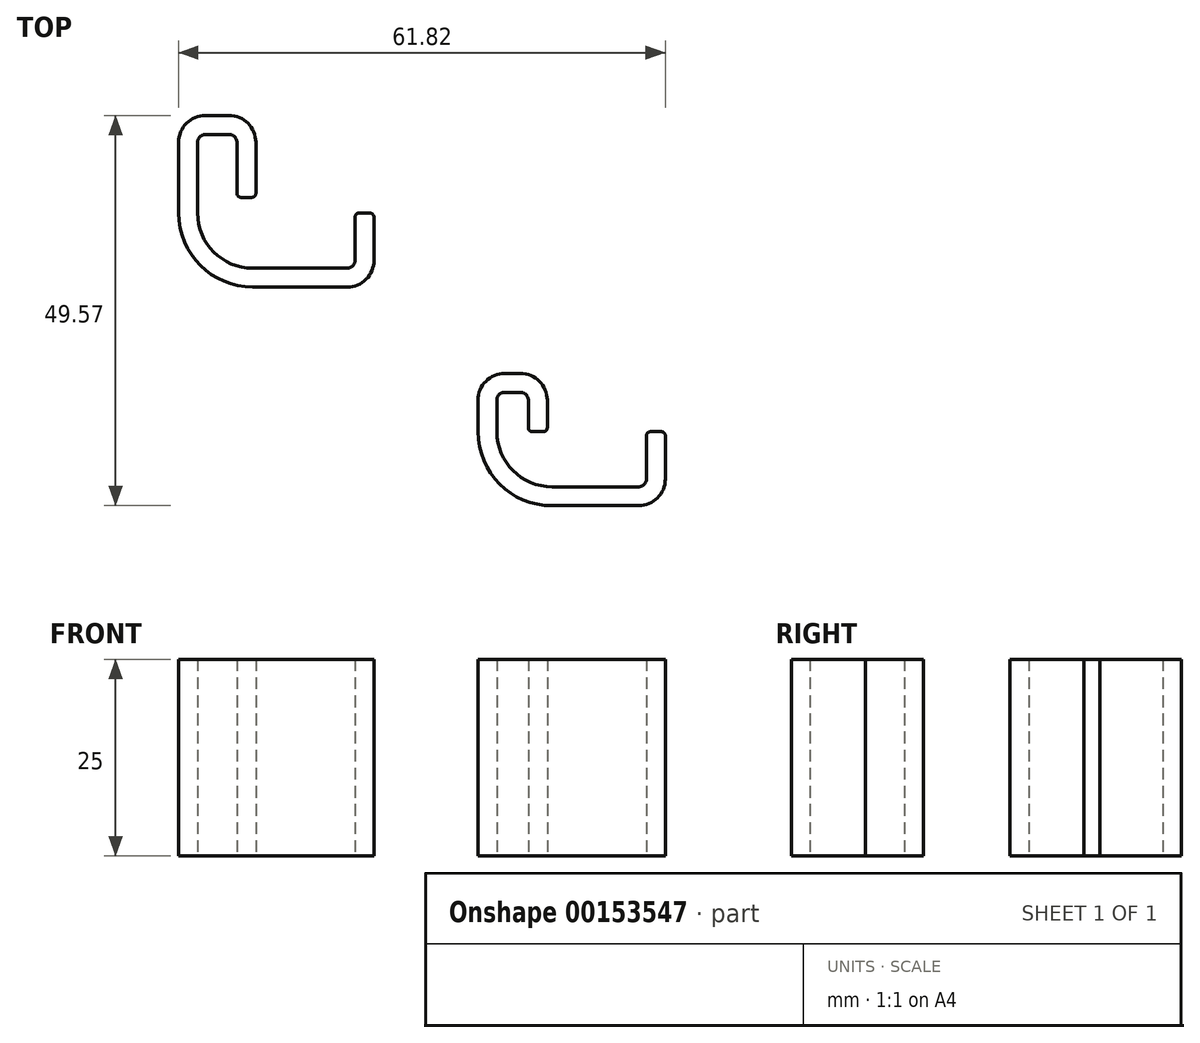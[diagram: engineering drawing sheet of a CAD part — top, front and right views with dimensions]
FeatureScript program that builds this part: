
annotation { "Feature Type Name" : "Feature", "Feature Type Description" : "" }
export const myFeature = defineFeature(function(context is Context, id is Id, definition is map)
    precondition{}
    {
        {
            var Q0;
            Q0=qCreatedBy(makeId("Top.planeOp"),FACE);
            var sketch = newSketch(context, id + "F0", { "sketchPlane" : qUnion([Q0])});
            skLineSegment(sketch, "E0", {"start": v(0, -0.5) * mm, "end": v(0, -6) * mm});
            skLineSegment(sketch, "E1", {"start": v(-1, -7) * mm, "end": v(-12, -7) * mm});
            skLineSegment(sketch, "E2", {"start": v(-15, 5) * mm, "end": v(-15, 0) * mm});
            skLineSegment(sketch, "E3", {"start": v(-15, 0.5) * mm, "end": v(-15, 4) * mm});
            skLineSegment(sketch, "E4", {"start": v(-16, 5) * mm, "end": v(-18, 5) * mm});
            skLineSegment(sketch, "E5", {"start": v(-19, 4) * mm, "end": v(-19, 0) * mm});
            skPoint(sketch, "E6.visualSharp", {"position": v(-19, -7) * mm});
            skArc(sketch, "E6.filletArc", {"start": v(-19, 0) * mm, "mid": v(-16.95, -4.95) * mm, "end": v(-12, -7) * mm});
            skPoint(sketch, "E7.visualSharp", {"position": v(-19, 5) * mm});
            skArc(sketch, "E7.filletArc", {"start": v(-18, 5) * mm, "mid": v(-18.7, 4.7) * mm, "end": v(-19, 4) * mm});
            skPoint(sketch, "E8.visualSharp", {"position": v(-15, 5) * mm});
            skArc(sketch, "E8.filletArc", {"start": v(-15, 4) * mm, "mid": v(-15.3, 4.7) * mm, "end": v(-16, 5) * mm});
            skPoint(sketch, "E9.visualSharp", {"position": v(0, -7) * mm});
            skArc(sketch, "E9.filletArc", {"start": v(-1, -7) * mm, "mid": v(-0.3, -6.7) * mm, "end": v(0, -6) * mm});
            skLineSegment(sketch, "E10.0", {"start": v(2.4, -0.5) * mm, "end": v(2.4, -6) * mm});
            skArc(sketch, "E10.1", {"start": v(-1, -9.4) * mm, "mid": v(1.4, -8.4) * mm, "end": v(2.4, -6) * mm});
            skLineSegment(sketch, "E10.2", {"start": v(-1, -9.4) * mm, "end": v(-12, -9.4) * mm});
            skArc(sketch, "E10.3", {"start": v(-21.4, 0) * mm, "mid": v(-18.65, -6.65) * mm, "end": v(-12, -9.4) * mm});
            skLineSegment(sketch, "E10.4", {"start": v(-21.4, 4) * mm, "end": v(-21.4, 0) * mm});
            skLineSegment(sketch, "E10.5", {"start": v(-12.6, 0.5) * mm, "end": v(-12.6, 4) * mm});
            skArc(sketch, "E10.6", {"start": v(-12.6, 4) * mm, "mid": v(-13.6, 6.4) * mm, "end": v(-16, 7.4) * mm});
            skLineSegment(sketch, "E10.7", {"start": v(-16, 7.4) * mm, "end": v(-18, 7.4) * mm});
            skArc(sketch, "E10.8", {"start": v(-18, 7.4) * mm, "mid": v(-20.4, 6.4) * mm, "end": v(-21.4, 4) * mm});
            skLineSegment(sketch, "E11", {"start": v(-13.1, 0) * mm, "end": v(-14.5, 0) * mm});
            skLineSegment(sketch, "E12", {"start": v(0.5, 0) * mm, "end": v(1.9, 0) * mm});
            skPoint(sketch, "E13.visualSharp", {"position": v(-15, 0) * mm});
            skArc(sketch, "E13.filletArc", {"start": v(-15, 0.5) * mm, "mid": v(-14.85, 0.15) * mm, "end": v(-14.5, 0) * mm});
            skPoint(sketch, "E14.visualSharp", {"position": v(-12.6, 0) * mm});
            skArc(sketch, "E14.filletArc", {"start": v(-13.1, 0) * mm, "mid": v(-12.75, 0.15) * mm, "end": v(-12.6, 0.5) * mm});
            skPoint(sketch, "E15.visualSharp", {"position": v(0, 0) * mm});
            skArc(sketch, "E15.filletArc", {"start": v(0.5, 0) * mm, "mid": v(0.15, -0.15) * mm, "end": v(0, -0.5) * mm});
            skPoint(sketch, "E16.visualSharp", {"position": v(2.4, 0) * mm});
            skArc(sketch, "E16.filletArc", {"start": v(2.4, -0.5) * mm, "mid": v(2.25, -0.15) * mm, "end": v(1.9, 0) * mm});
            skSolve(sketch);
        }
        {
            var Q0;
            Q0=qCreatedBy(makeId("Top.planeOp"),FACE);
            var sketch = newSketch(context, id + "F1", { "sketchPlane" : qUnion([Q0])});
            skLineSegment(sketch, "E17", {"start": v(-37.02, 27.27) * mm, "end": v(-37.02, 21.77) * mm});
            skLineSegment(sketch, "E18", {"start": v(-38.02, 20.77) * mm, "end": v(-50.02, 20.77) * mm});
            skLineSegment(sketch, "E19", {"start": v(-52.02, 37.77) * mm, "end": v(-52.02, 29.77) * mm});
            skLineSegment(sketch, "E20", {"start": v(-52.02, 30.27) * mm, "end": v(-52.02, 36.77) * mm});
            skLineSegment(sketch, "E21", {"start": v(-53.02, 37.77) * mm, "end": v(-56.02, 37.77) * mm});
            skLineSegment(sketch, "E22", {"start": v(-57.02, 36.77) * mm, "end": v(-57.02, 27.77) * mm});
            skPoint(sketch, "E23.visualSharp", {"position": v(-57.02, 20.77) * mm});
            skArc(sketch, "E23.filletArc", {"start": v(-57.02, 27.77) * mm, "mid": v(-54.97, 22.82) * mm, "end": v(-50.02, 20.77) * mm});
            skPoint(sketch, "E24.visualSharp", {"position": v(-57.02, 37.77) * mm});
            skArc(sketch, "E24.filletArc", {"start": v(-56.02, 37.77) * mm, "mid": v(-56.72, 37.48) * mm, "end": v(-57.02, 36.77) * mm});
            skPoint(sketch, "E25.visualSharp", {"position": v(-52.02, 37.77) * mm});
            skArc(sketch, "E25.filletArc", {"start": v(-52.02, 36.77) * mm, "mid": v(-52.3, 37.48) * mm, "end": v(-53.02, 37.77) * mm});
            skPoint(sketch, "E26.visualSharp", {"position": v(-37.02, 20.77) * mm});
            skArc(sketch, "E26.filletArc", {"start": v(-38.02, 20.77) * mm, "mid": v(-37.3, 21.06) * mm, "end": v(-37.02, 21.77) * mm});
            skLineSegment(sketch, "E27.0", {"start": v(-34.62, 27.27) * mm, "end": v(-34.62, 21.77) * mm});
            skArc(sketch, "E27.1", {"start": v(-38.02, 18.37) * mm, "mid": v(-35.61, 19.37) * mm, "end": v(-34.62, 21.77) * mm});
            skLineSegment(sketch, "E27.2", {"start": v(-38.02, 18.37) * mm, "end": v(-50.02, 18.37) * mm});
            skArc(sketch, "E27.3", {"start": v(-59.42, 27.77) * mm, "mid": v(-56.66, 21.12) * mm, "end": v(-50.02, 18.37) * mm});
            skLineSegment(sketch, "E27.4", {"start": v(-59.42, 36.77) * mm, "end": v(-59.42, 27.77) * mm});
            skLineSegment(sketch, "E27.5", {"start": v(-49.62, 30.27) * mm, "end": v(-49.62, 36.77) * mm});
            skArc(sketch, "E27.6", {"start": v(-49.62, 36.77) * mm, "mid": v(-50.61, 39.17) * mm, "end": v(-53.02, 40.17) * mm});
            skLineSegment(sketch, "E27.7", {"start": v(-53.02, 40.17) * mm, "end": v(-56.02, 40.17) * mm});
            skArc(sketch, "E27.8", {"start": v(-56.02, 40.17) * mm, "mid": v(-58.42, 39.17) * mm, "end": v(-59.42, 36.77) * mm});
            skLineSegment(sketch, "E28", {"start": v(-50.12, 29.77) * mm, "end": v(-51.52, 29.77) * mm});
            skLineSegment(sketch, "E29", {"start": v(-36.52, 27.77) * mm, "end": v(-35.12, 27.77) * mm});
            skPoint(sketch, "E30.visualSharp", {"position": v(-52.02, 29.77) * mm});
            skArc(sketch, "E30.filletArc", {"start": v(-52.02, 30.27) * mm, "mid": v(-51.87, 29.92) * mm, "end": v(-51.52, 29.77) * mm});
            skPoint(sketch, "E31.visualSharp", {"position": v(-49.62, 29.77) * mm});
            skArc(sketch, "E31.filletArc", {"start": v(-50.12, 29.77) * mm, "mid": v(-49.76, 29.92) * mm, "end": v(-49.62, 30.27) * mm});
            skPoint(sketch, "E32.visualSharp", {"position": v(-37.02, 27.77) * mm});
            skArc(sketch, "E32.filletArc", {"start": v(-36.52, 27.77) * mm, "mid": v(-36.87, 27.62) * mm, "end": v(-37.02, 27.27) * mm});
            skPoint(sketch, "E33.visualSharp", {"position": v(-34.62, 27.77) * mm});
            skArc(sketch, "E33.filletArc", {"start": v(-34.62, 27.27) * mm, "mid": v(-34.76, 27.62) * mm, "end": v(-35.12, 27.77) * mm});
            skSolve(sketch);
        }
        {
            var Q0;
            Q0 = qSketchRegion(id + "F0", true);
            var Q1;
            Q1 = qSketchRegion(id + "F1", true);
            extrude(context, id + "F2", {"entities" : qUnion([Q0, Q1]), "depth" : 25 * mm});
        }
    });
